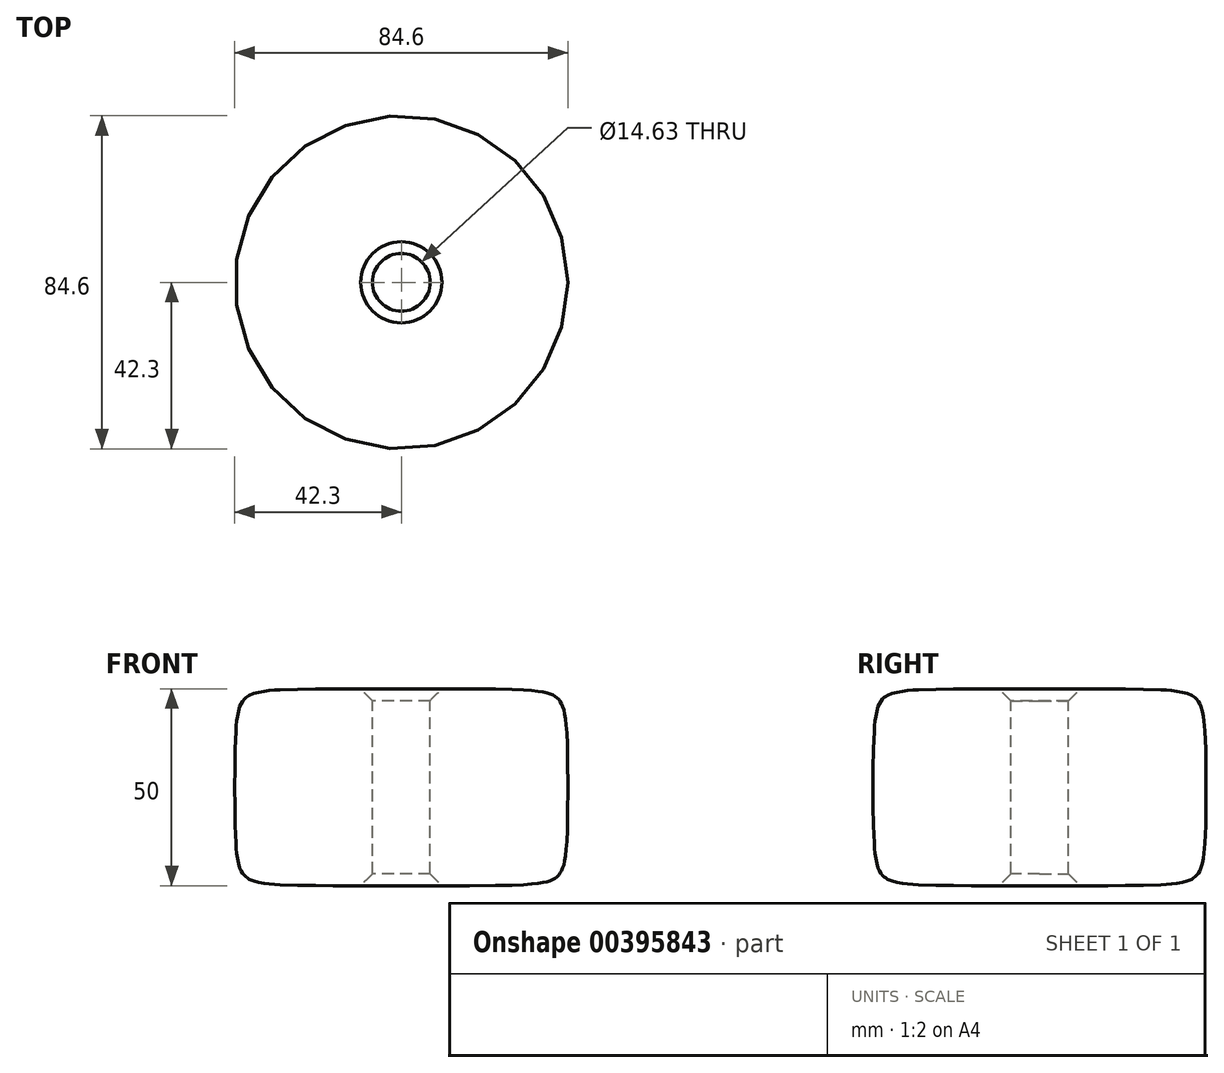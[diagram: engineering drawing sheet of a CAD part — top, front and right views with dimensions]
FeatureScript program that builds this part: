
annotation { "Feature Type Name" : "Feature", "Feature Type Description" : "" }
export const myFeature = defineFeature(function(context is Context, id is Id, definition is map)
    precondition{}
    {
        {
            var Q0;
            Q0=qCreatedBy(makeId("Top.planeOp"),FACE);
            var sketch = newSketch(context, id + "F0", { "sketchPlane" : qUnion([Q0])});
            skCircle(sketch, "E0", {"center": v(0, 0) * mm, "radius": 42.3 * mm});
            skSolve(sketch);
        }
        {
            var Q0;
            Q0=makeQuery(id+"F0.imprint","IMPRINT",FACE,{"disambiguationData":[TD([[makeQuery(id+"F0.imprint","IMPRINT",EDGE,{"derivedFrom":sQuery(id+"F0.wireOp",EDGE,"E0")}),1.0]])]});
            extrude(context, id + "F1", {"entities" : qUnion([Q0]), "depth" : 25 * mm});
        }
        {
            var Q0;
            Q0=makeQuery(id+"F1.opExtrude","CAP_EDGE",EDGE,{"disambiguationData":[OSD([sQuery(id+"F0.wireOp",EDGE,"E0")])],"isStart":false});
            fillet(context, id + "F2", {"entities" : qUnion([Q0]), "radius" : 25 * mm, "tangentPropagation" : true, "rho" : .8, "crossSection" : FilletCrossSection.CONIC, "allowEdgeOverflow" : false});
        }
        {
            var Q0;
            Q0=makeQuery(id+"F1.opExtrude","SWEPT_BODY",BODY,{"disambiguationData":[OSD([sQuery(id+"F0.wireOp",EDGE,"E0")])]});
            var Q1;
            Q1=makeQuery(id+"F1.opExtrude","CAP_FACE",FACE,{"disambiguationData":[OSD([sQuery(id+"F0.wireOp",EDGE,"E0")])],"isStart":true});
            mirror(context, id + "F3", {"operationType" : NewBodyOperationType.ADD, "entities" : qUnion([Q0]), "mirrorPlane" : qUnion([Q1])});
        }
        {
            var Q0;
            Q0=makeQuery(id+"F1.opExtrude","CAP_FACE",FACE,{"disambiguationData":[OSD([sQuery(id+"F0.wireOp",EDGE,"E0")])],"isStart":false});
            var sketch = newSketch(context, id + "F4", { "sketchPlane" : qUnion([Q0])});
            skCircle(sketch, "E1", {"center": v(0, 0) * mm, "radius": 7.31 * mm});
            skSolve(sketch);
        }
        {
            var Q0;
            Q0=makeQuery(id+"F4.imprint","IMPRINT",FACE,{"disambiguationData":[TD([[makeQuery(id+"F4.imprint","IMPRINT",EDGE,{"derivedFrom":sQuery(id+"F4.wireOp",EDGE,"E1")}),1.0]])]});
            extrude(context, id + "F5", {"entities" : qUnion([Q0]), "operationType" : NewBodyOperationType.REMOVE, "endBound" : BoundingType.THROUGH_ALL, "oppositeDirection" : true, "depth" : 25 * mm});
        }
        {
            var Q0;
            Q0=makeQuery(id+"F5.boolean.opBoolean","COPY",FACE,{"derivedFrom":makeQuery(id+"F5.opExtrude","SWEPT_FACE",FACE,{"disambiguationData":[OSD([sQuery(id+"F4.wireOp",EDGE,"E1")])]})});
            chamfer(context, id + "F6", {"entities" : qUnion([Q0]), "width" : 3 * mm, "tangentPropagation" : true});
        }
    });
